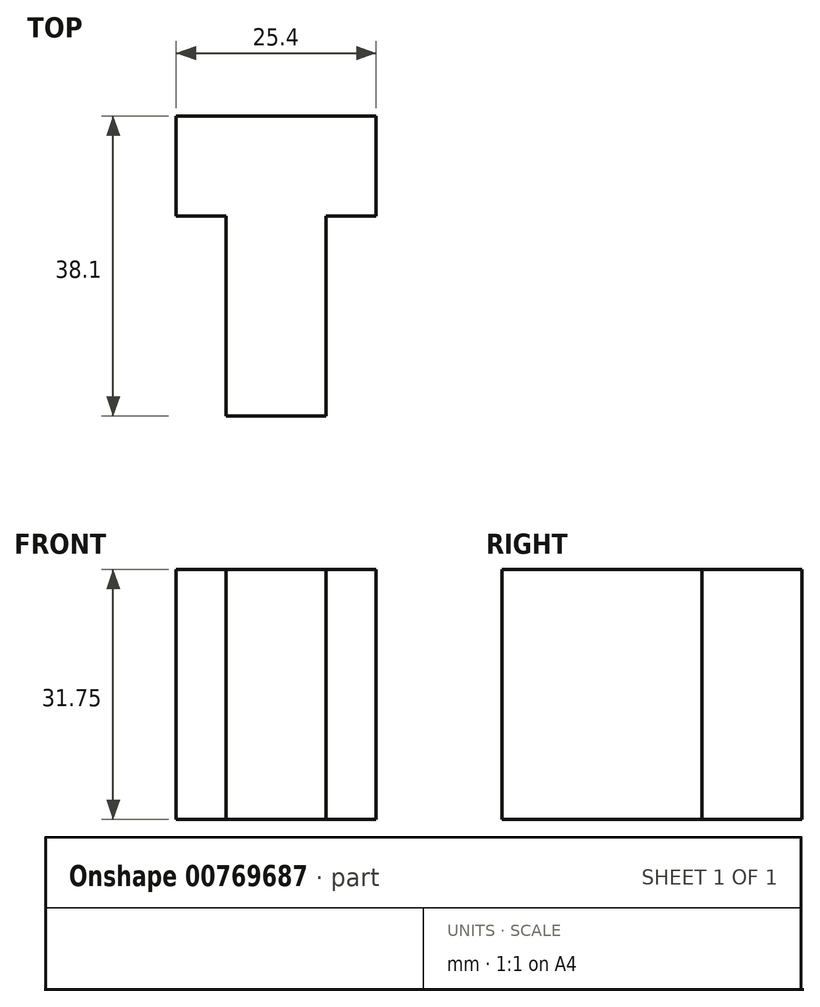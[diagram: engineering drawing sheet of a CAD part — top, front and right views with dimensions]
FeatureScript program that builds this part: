
annotation { "Feature Type Name" : "Feature", "Feature Type Description" : "" }
export const myFeature = defineFeature(function(context is Context, id is Id, definition is map)
    precondition{}
    {
        {
            var Q0;
            Q0=qCreatedBy(makeId("Top.planeOp"),FACE);
            var sketch = newSketch(context, id + "F0", { "sketchPlane" : qUnion([Q0])});
            skLineSegment(sketch, "E0", {"start": v(0, 0) * mm, "end": v(6.35, 0) * mm});
            skLineSegment(sketch, "E1", {"start": v(6.35, 0) * mm, "end": v(6.35, -25.4) * mm});
            skLineSegment(sketch, "E2", {"start": v(6.35, -25.4) * mm, "end": v(19.05, -25.4) * mm});
            skLineSegment(sketch, "E3", {"start": v(19.05, -25.4) * mm, "end": v(19.05, 0) * mm});
            skLineSegment(sketch, "E4", {"start": v(19.05, 0) * mm, "end": v(25.4, 0) * mm});
            skLineSegment(sketch, "E5", {"start": v(25.4, 0) * mm, "end": v(25.4, 12.7) * mm});
            skLineSegment(sketch, "E6", {"start": v(25.4, 12.7) * mm, "end": v(0, 12.7) * mm});
            skLineSegment(sketch, "E7", {"start": v(0, 12.7) * mm, "end": v(0, 0) * mm});
            skSolve(sketch);
        }
        {
            var Q0;
            Q0=makeQuery(id+"F0.imprint","IMPRINT",FACE,{"disambiguationData":[TD([[makeQuery(id+"F0.imprint","IMPRINT",EDGE,{"derivedFrom":sQuery(id+"F0.wireOp",EDGE,"E0")}),1.0]])]});
            extrude(context, id + "F1", {"entities" : qUnion([Q0]), "depth" : 31.75 * mm, "offsetDistance" : 25.4 * mm});
        }
    });
